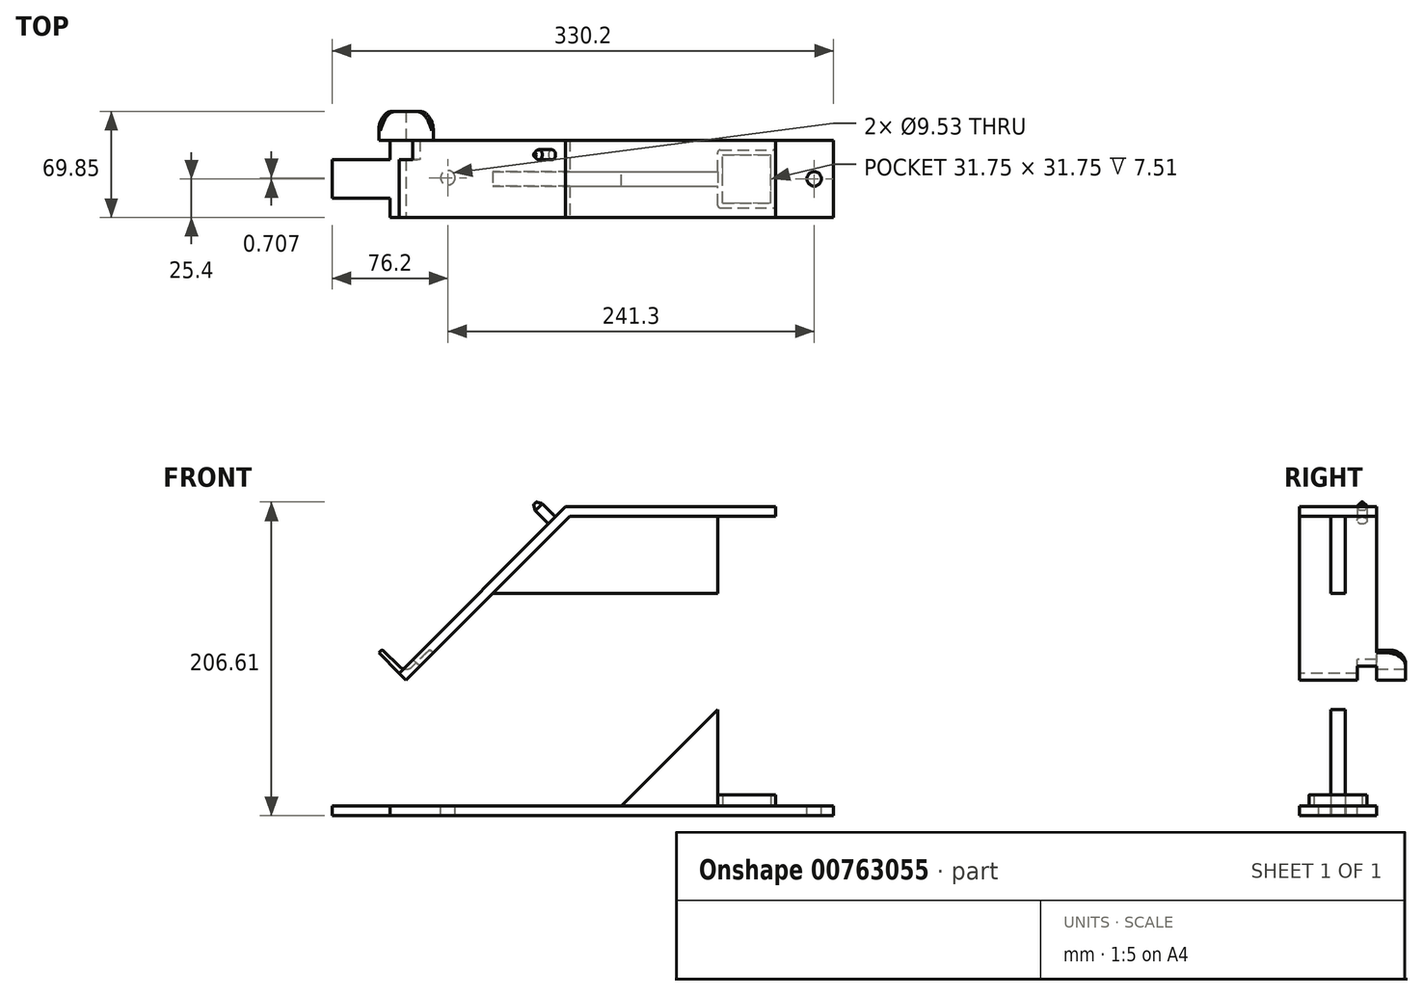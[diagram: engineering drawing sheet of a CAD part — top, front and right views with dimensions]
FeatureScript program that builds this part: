
annotation { "Feature Type Name" : "Feature", "Feature Type Description" : "" }
export const myFeature = defineFeature(function(context is Context, id is Id, definition is map)
    precondition{}
    {
        {
            assignVariable(context, id + "F0", {"name" : "haut", "anyValue" : 8 - 0.49});
        }
        {
            var Q0;
            Q0=qCreatedBy(makeId("Top.planeOp"),FACE);
            var sketch = newSketch(context, id + "F1", { "sketchPlane" : qUnion([Q0])});
            skLineSegment(sketch, "E0.bottom", {"start": v(0, 0) * mm, "end": v(114.3, 0) * mm});
            skLineSegment(sketch, "E0.top", {"start": v(0, 50.8) * mm, "end": v(114.3, 50.8) * mm});
            skLineSegment(sketch, "E0.left", {"start": v(0, 0) * mm, "end": v(0, 50.8) * mm});
            skLineSegment(sketch, "E0.right", {"start": v(114.3, 0) * mm, "end": v(114.3, 50.8) * mm});
            skLineSegment(sketch, "E1.bottom", {"start": v(0, 0) * mm, "end": v(-177.8, 0) * mm});
            skLineSegment(sketch, "E1.top", {"start": v(0, 50.8) * mm, "end": v(-177.8, 50.8) * mm});
            skLineSegment(sketch, "E1.right", {"start": v(-215.9, 12.7) * mm, "end": v(-215.9, 38.1) * mm});
            skLineSegment(sketch, "E2.top", {"start": v(-215.9, 38.1) * mm, "end": v(-177.8, 38.1) * mm});
            skLineSegment(sketch, "E2.right", {"start": v(-177.8, 50.8) * mm, "end": v(-177.8, 38.1) * mm});
            skLineSegment(sketch, "E3.top", {"start": v(-215.9, 12.7) * mm, "end": v(-177.8, 12.7) * mm});
            skLineSegment(sketch, "E3.right", {"start": v(-177.8, 0) * mm, "end": v(-177.8, 12.7) * mm});
            skCircle(sketch, "E4", {"center": v(101.6, 25.4) * mm, "radius": 4.76 * mm});
            skCircle(sketch, "E5", {"center": v(-139.7, 26.1) * mm, "radius": 4.76 * mm});
            skSolve(sketch);
        }
        {
            var Q0;
            Q0 = qSketchRegion(id + "F1", true);
            extrude(context, id + "F2", {"entities" : qUnion([Q0]), "oppositeDirection" : true, "depth" : 6.35 * mm, "offsetDistance" : 25.4 * mm});
        }
        {
            var Q0;
            Q0=makeQuery(id+"F2.opExtrude","CAP_FACE",FACE,{"disambiguationData":[OSD([sQuery(id+"F1.wireOp",EDGE,"E0.bottom"),sQuery(id+"F1.wireOp",EDGE,"E0.top"),sQuery(id+"F1.wireOp",EDGE,"E0.left"),sQuery(id+"F1.wireOp",EDGE,"E0.right")])],"isStart":true});
            var sketch = newSketch(context, id + "F3", { "sketchPlane" : qUnion([Q0])});
            skLineSegment(sketch, "E6.bottom", {"start": v(38.1, 6.35) * mm, "end": v(76.2, 6.35) * mm});
            skLineSegment(sketch, "E6.top", {"start": v(38.1, 44.45) * mm, "end": v(76.2, 44.45) * mm});
            skLineSegment(sketch, "E6.left", {"start": v(38.1, 6.35) * mm, "end": v(38.1, 44.45) * mm});
            skLineSegment(sketch, "E6.right", {"start": v(76.2, 6.35) * mm, "end": v(76.2, 44.45) * mm});
            skLineSegment(sketch, "E7.0", {"start": v(41.27, 41.28) * mm, "end": v(73.03, 41.28) * mm});
            skLineSegment(sketch, "E7.1", {"start": v(41.27, 9.52) * mm, "end": v(41.27, 41.28) * mm});
            skLineSegment(sketch, "E7.2", {"start": v(41.27, 9.52) * mm, "end": v(73.03, 9.53) * mm});
            skLineSegment(sketch, "E7.3", {"start": v(73.03, 9.53) * mm, "end": v(73.03, 41.28) * mm});
            skSolve(sketch);
        }
        {
            var Q0;
            Q0 = qSketchRegion(id + "F3", true);
            extrude(context, id + "F4", {"entities" : qUnion([Q0]), "operationType" : NewBodyOperationType.ADD, "depth" : (getVariable(context, 'haut')) * mm, "offsetDistance" : 25.4 * mm});
        }
        {
            var Q0;
            Q0=makeQuery(id+"F4.opExtrude","SWEPT_FACE",FACE,{"disambiguationData":[OSD([sQuery(id+"F3.wireOp",EDGE,"E6.bottom")])]});
            var sketch = newSketch(context, id + "F5", { "sketchPlane" : qUnion([Q0])});
            skLineSegment(sketch, "E8", {"start": v(76.2, 190.76) * mm, "end": v(-59.52, 190.76) * mm});
            skLineSegment(sketch, "E9", {"start": v(-59.52, 190.76) * mm, "end": v(-167.28, 83) * mm});
            skLineSegment(sketch, "E10.0", {"start": v(76.2, 197.11) * mm, "end": v(-62.15, 197.11) * mm});
            skLineSegment(sketch, "E11.0", {"start": v(-62.15, 197.11) * mm, "end": v(-171.77, 87.5) * mm});
            skLineSegment(sketch, "E12", {"start": v(-167.28, 83) * mm, "end": v(-171.77, 87.5) * mm});
            skLineSegment(sketch, "E13", {"start": v(76.2, 190.76) * mm, "end": v(76.2, 197.11) * mm});
            skSolve(sketch);
        }
        {
            var Q0;
            Q0 = qSketchRegion(id + "F5", true);
            extrude(context, id + "F6", {"entities" : qUnion([Q0]), "operationType" : NewBodyOperationType.ADD, "oppositeDirection" : true, "depth" : 44.45 * mm, "offsetDistance" : 25.4 * mm, "hasSecondDirection" : true, "secondDirectionOppositeDirection" : false, "secondDirectionDepth" : 6.35 * mm});
        }
        {
            var Q0;
            Q0=makeQuery(id+"F6.opExtrude","SWEPT_FACE",FACE,{"disambiguationData":[OSD([sQuery(id+"F5.wireOp",EDGE,"E11.0")])]});
            var sketch = newSketch(context, id + "F7", { "sketchPlane" : qUnion([Q0])});
            skCircle(sketch, "E14", {"center": v(-41.28, 82.74) * mm, "radius": 3.3 * mm});
            skLineSegment(sketch, "E15.direction1", {"start": v(-41.28, 82.74) * mm, "end": v(-15.88, 82.74) * mm, "construction": true});
            skLineSegment(sketch, "E15.direction2", {"start": v(-41.28, 82.74) * mm, "end": v(-41.28, -44.26) * mm, "construction": true});
            skSolve(sketch);
        }
        {
            var Q0;
            Q0 = qSketchRegion(id + "F7", true);
            extrude(context, id + "F8", {"entities" : qUnion([Q0]), "operationType" : NewBodyOperationType.ADD, "depth" : 15.88 * mm, "offsetDistance" : 25.4 * mm});
        }
        {
            var Q0;
            Q0=makeQuery(id+"F8.opExtrude","CAP_EDGE",EDGE,{"disambiguationData":[OSD([sQuery(id+"F7.wireOp",EDGE,"E14")])],"isStart":false});
            var Q1;
            Q1=makeQuery(id+"F8.opExtrude","CAP_EDGE",EDGE,{"disambiguationData":[OSD([sQuery(id+"F7.wireOp",EDGE,"E15.0.1.0")])],"isStart":false});
            chamfer(context, id + "F9", {"entities" : qUnion([Q0, Q1]), "chamferType" : ChamferType.OFFSET_ANGLE, "width" : 2.03 * mm, "oppositeDirection" : false, "angle" : 60 * degree, "tangentPropagation" : true});
        }
        {
            var Q0;
            Q0=makeQuery(id+"F7.imprint","IMPRINT",FACE,{"disambiguationData":[TD([[makeQuery(id+"F7.imprint","IMPRINT",EDGE,{"derivedFrom":sQuery(id+"F7.wireOp",EDGE,"E14")}),-1.0]])]});
            var sketch = newSketch(context, id + "F10", { "sketchPlane" : qUnion([Q0])});
            skLineSegment(sketch, "E16.bottom", {"start": v(-50.8, -59.6) * mm, "end": v(-38.1, -59.6) * mm});
            skLineSegment(sketch, "E16.top", {"start": v(-50.8, -46.9) * mm, "end": v(-38.1, -46.9) * mm});
            skLineSegment(sketch, "E16.left", {"start": v(-50.8, -59.6) * mm, "end": v(-50.8, -46.9) * mm});
            skLineSegment(sketch, "E16.right", {"start": v(-38.1, -59.6) * mm, "end": v(-38.1, -46.9) * mm});
            skSolve(sketch);
        }
        {
            var Q0;
            Q0 = qSketchRegion(id + "F10", true);
            extrude(context, id + "F11", {"entities" : qUnion([Q0]), "operationType" : NewBodyOperationType.REMOVE, "oppositeDirection" : true, "depth" : 25.4 * mm, "offsetDistance" : 25.4 * mm});
        }
        {
            var Q0;
            Q0=makeQuery(id+"F6.opExtrude","CAP_FACE",FACE,{"disambiguationData":[OSD([sQuery(id+"F5.wireOp",EDGE,"E8"),sQuery(id+"F5.wireOp",EDGE,"E9"),sQuery(id+"F5.wireOp",EDGE,"E10.0"),sQuery(id+"F5.wireOp",EDGE,"E11.0"),sQuery(id+"F5.wireOp",EDGE,"E12"),sQuery(id+"F5.wireOp",EDGE,"E13")])],"isStart":false});
            var sketch = newSketch(context, id + "F12", { "sketchPlane" : qUnion([Q0])});
            skLineSegment(sketch, "E17", {"start": v(149.32, 100.96) * mm, "end": v(167.28, 83) * mm});
            skLineSegment(sketch, "E18", {"start": v(149.32, 100.96) * mm, "end": v(151.56, 103.2) * mm});
            skLineSegment(sketch, "E19", {"start": v(167.28, 83) * mm, "end": v(185.24, 100.96) * mm});
            skLineSegment(sketch, "E20.0", {"start": v(151.56, 103.2) * mm, "end": v(167.28, 87.5) * mm});
            skLineSegment(sketch, "E21.0", {"start": v(167.28, 87.5) * mm, "end": v(183, 103.2) * mm});
            skLineSegment(sketch, "E22.0", {"start": v(183, 103.2) * mm, "end": v(185.24, 100.96) * mm});
            skSolve(sketch);
        }
        {
            var Q0;
            Q0 = qSketchRegion(id + "F12", true);
            extrude(context, id + "F13", {"entities" : qUnion([Q0]), "operationType" : NewBodyOperationType.ADD, "depth" : 19.05 * mm, "offsetDistance" : 25.4 * mm});
        }
        {
            var Q0;
            Q0=makeQuery(id+"F13.opExtrude","CAP_EDGE",EDGE,{"disambiguationData":[OSD([sQuery(id+"F12.wireOp",EDGE,"E22.0")])],"isStart":false});
            fillet(context, id + "F14", {"entities" : qUnion([Q0]), "radius" : 12.7 * mm, "tangentPropagation" : true, "allowEdgeOverflow" : false});
        }
        {
            var Q0;
            Q0=makeQuery(id+"F13.opExtrude","CAP_EDGE",EDGE,{"disambiguationData":[OSD([sQuery(id+"F12.wireOp",EDGE,"E18")])],"isStart":false});
            fillet(context, id + "F15", {"entities" : qUnion([Q0]), "radius" : 12.7 * mm, "tangentPropagation" : true, "allowEdgeOverflow" : false});
        }
        {
            var Q0;
            Q0=makeQuery(id+"F13.opExtrude","SWEPT_EDGE",EDGE,{"disambiguationData":[OSD([sQuery(id+"F12.wireOp",EDGE,"E20.0"),sQuery(id+"F12.wireOp",EDGE,"E21.0")])]});
            fillet(context, id + "F16", {"entities" : qUnion([Q0]), "radius" : 6.35 * mm, "tangentPropagation" : true, "allowEdgeOverflow" : false});
        }
        {
            var Q0;
            Q0=makeQuery(id+"F13.opExtrude","SWEPT_EDGE",EDGE,{"disambiguationData":[OSD([sQuery(id+"F12.wireOp",EDGE,"E21.0"),sQuery(id+"F12.wireOp",EDGE,"E22.0")])]});
            var Q1;
            Q1=makeQuery(id+"F13.opExtrude","SWEPT_EDGE",EDGE,{"disambiguationData":[OSD([sQuery(id+"F12.wireOp",EDGE,"E18"),sQuery(id+"F12.wireOp",EDGE,"E20.0")])]});
            fillet(context, id + "F17", {"entities" : qUnion([Q0, Q1]), "radius" : 1.59 * mm, "allowEdgeOverflow" : false});
        }
        {
            var Q0;
            Q0=makeQuery(id+"F4.opExtrude","SWEPT_FACE",FACE,{"disambiguationData":[OSD([sQuery(id+"F3.wireOp",EDGE,"E6.left")])]});
            var sketch = newSketch(context, id + "F18", { "sketchPlane" : qUnion([Q0])});
            skLineSegment(sketch, "E23.bottom", {"start": v(-30.16, 190.76) * mm, "end": v(-20.64, 190.76) * mm});
            skLineSegment(sketch, "E23.top", {"start": v(-30.16, 139.96) * mm, "end": v(-20.64, 139.96) * mm});
            skLineSegment(sketch, "E23.left", {"start": v(-30.16, 190.76) * mm, "end": v(-30.16, 139.96) * mm});
            skLineSegment(sketch, "E23.right", {"start": v(-20.64, 190.76) * mm, "end": v(-20.64, 139.96) * mm});
            skSolve(sketch);
        }
        {
            var Q0;
            Q0 = qSketchRegion(id + "F18", true);
            extrude(context, id + "F19", {"entities" : qUnion([Q0]), "operationType" : NewBodyOperationType.ADD, "endBound" : BoundingType.UP_TO_NEXT, "depth" : 25.4 * mm, "offsetDistance" : 25.4 * mm});
        }
        {
            var Q0;
            Q0=makeQuery(id+"F4.opExtrude","SWEPT_EDGE",EDGE,{"disambiguationData":[OSD([sQuery(id+"F3.wireOp",EDGE,"E6.bottom"),sQuery(id+"F3.wireOp",EDGE,"E6.right")])]});
            var Q1;
            Q1=makeQuery(id+"F4.opExtrude","SWEPT_EDGE",EDGE,{"disambiguationData":[OSD([sQuery(id+"F3.wireOp",EDGE,"E6.bottom"),sQuery(id+"F3.wireOp",EDGE,"E6.left")])]});
            var Q2;
            Q2=makeQuery(id+"F4.opExtrude","SWEPT_EDGE",EDGE,{"disambiguationData":[OSD([sQuery(id+"F3.wireOp",EDGE,"E6.top"),sQuery(id+"F3.wireOp",EDGE,"E6.right")])]});
            var Q3;
            Q3=makeQuery(id+"F4.opExtrude","SWEPT_EDGE",EDGE,{"disambiguationData":[OSD([sQuery(id+"F3.wireOp",EDGE,"E6.top"),sQuery(id+"F3.wireOp",EDGE,"E6.left")])]});
            fillet(context, id + "F20", {"entities" : qUnion([Q0, Q1, Q2, Q3]), "radius" : 1.59 * mm, "tangentPropagation" : true, "allowEdgeOverflow" : false});
        }
        {
            var Q0;
            Q0=qCreatedBy(makeId("Front.planeOp"),FACE);
            cPlane(context, id + "F21", {"entities" : qUnion([Q0]), "cplaneType" : CPlaneType.OFFSET, "offset" : 25.4 * mm, "oppositeDirection" : true, "width" : 152.4 * mm, "height" : 152.4 * mm});
        }
        {
            var Q0;
            Q0=qCreatedBy(id+"F21.planeOp",FACE);
            var sketch = newSketch(context, id + "F22", { "sketchPlane" : qUnion([Q0])});
            skLineSegment(sketch, "E24", {"start": v(38.1, 63.5) * mm, "end": v(-25.4, 0) * mm});
            skLineSegment(sketch, "E25", {"start": v(38.1, 63.5) * mm, "end": v(38.1, 0) * mm});
            skLineSegment(sketch, "E26", {"start": v(-25.4, 0) * mm, "end": v(38.1, 0) * mm});
            skSolve(sketch);
        }
        {
            var Q0;
            Q0 = qSketchRegion(id + "F22", true);
            extrude(context, id + "F23", {"entities" : qUnion([Q0]), "operationType" : NewBodyOperationType.ADD, "depth" : 4.76 * mm, "offsetDistance" : 25.4 * mm, "hasSecondDirection" : true, "secondDirectionOppositeDirection" : true, "secondDirectionDepth" : 4.76 * mm});
        }
    });
